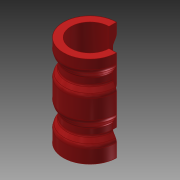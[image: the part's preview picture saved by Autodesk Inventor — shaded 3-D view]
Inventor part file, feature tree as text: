
AUTODESK INVENTOR PART (.ipt)
format: ipt  version: 2014 SP1 (Build 180222100, 222)  size: 167,936 bytes
history: native  units: in
note: dims shown in document units (in); Inventor stores cm internally (conversion verified against a paired STEP export)
features: revolve x1, fillet x1, sketch x1
ambient origin geometry x8: Origin, YZ Plane, XZ Plane, XY Plane, X Axis, Y Axis, Z Axis, Center Point
bodies: Solid1 (feature_tree)
feature tree (3):
  revolve  "Revolution1"  [1 undecoded]
  fillet  "Fillet1"  Radius=0.25in
  sketch  "Sketch1"  dims[d0=1.25in d1=0.5in d2=0.25in d3=150.0deg d4=0.75in d5=6.0in d6=150.0deg d7=0.5in d8=1.0in d9=6.0in d10=270.0deg d11=0.5in d12=0.25in]
note: 1 required parameter value undecoded (feature->parameter linkage not recoverable at this tier; creation-order binding heuristic only, values carry confidence <= 0.55)
